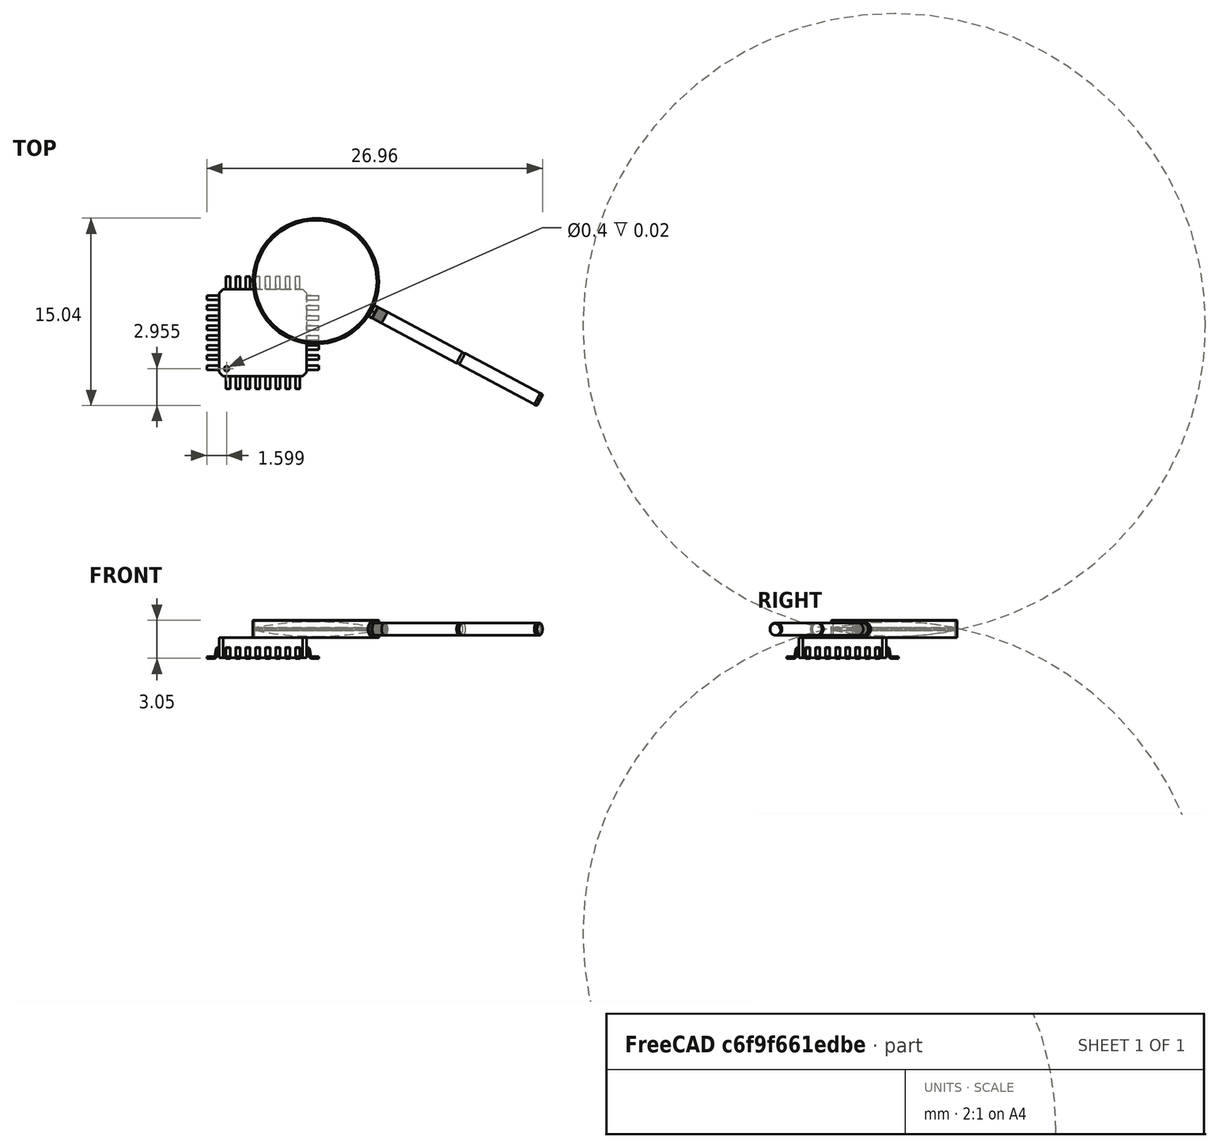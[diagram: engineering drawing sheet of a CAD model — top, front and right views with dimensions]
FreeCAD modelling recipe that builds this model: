
FCSTD DOCUMENT  (FreeCAD 0.16R6703 (Git))
Label: PQFP-033-atmega-328p
License: CC-BY 3.0
LicenseURL: http://creativecommons.org/licenses/by/3.0/
objects: Part::Feature×3, Part::Compound×2, Part::FeaturePython×1
note: 6 computed .brp shape members not serialized (recipe doc carries the construction recipe); baked Part::Feature solids carry a one-line shape summary decoded from their .brp

FEATURE [Part::Compound] Compound019  label="PQFP-033"
  Placement = pos=(-5.71099,-9.13488,1.7) rot=(0,0,1;0rad)
FEATURE [Part::Feature] Part__Feature  label="100mm Magnifying Glass"
  shape: bbox 108 x 11.7 x 108 mm, 14 faces (baked)
FEATURE [Part::Feature] Part__Feature001  label="100mm Magnifying Glass001"
  shape: bbox 113.6 x 14 x 101 mm, 77 faces (baked)
FEATURE [Part::Feature] Part__Feature002  label="100mm Magnifying Glass002"
  shape: bbox 150.3 x 11.24 x 11.24 mm, 25 faces (baked)
FEATURE [Part::Compound] Compound
  Links = -> [Part__Feature,Part__Feature001,Part__Feature002]
  Placement = pos=(0,0,0) rot=(1,0,0;1.5708rad)
FEATURE [Part::FeaturePython] Clone  label="Clone of Compound"  # Draft clone (typed FeaturePython)
  Objects = -> [Compound]
  Placement = pos=(3.06983,-0.504728,4) rot=(0.94309,-0.235139,-0.235139;1.62936rad)
  Scale = (0.1,0.1,0.1)
